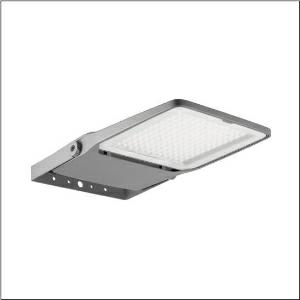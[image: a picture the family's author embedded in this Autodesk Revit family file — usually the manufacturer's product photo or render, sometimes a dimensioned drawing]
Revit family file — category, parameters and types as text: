
# Revit family: floodlight_fl_20_midi___pl52_5xa7682e2d2ac_72a0
name_source: partatom
category: Lighting Fixtures
units: mm (PartAtom-declared; Revit-internal decimal feet)

## family parameters
Cut with Voids When Loaded = No
Host = Face
Light Source = No
Part Type = Normal
Room Calculation Point = No
Round Connector Dimension = Use Diameter
Shared = No

## types (1)
- --- (1 x LED 4000K / CRI = 70 (unbekannt), 26840 lm, 4000K)
    Apparent Load = 208 VA
    CIE Flux Codes = 27 59 98 100 100
    Color Rendering = 70
    Color Temperature = 4000K
    Default Elevation = 1800 mm
    Description = Floodlight FL 20 midi, floodlight, primary light control with lens, of plastic, primary optical cover: protective disc, of toughened safety glass, transparent, light distribution: PL52, light emission: direct distribution, primary light characteristic: asymmetric, installation type: surface-mounted, LED High Power LED, rated luminous flux: 26.840 lm, light colour: 740, colour temperature: 4000K, control gear: ECG Plus, control: flexible luminous flux parameterisation, time-dependent luminous flux control, digital communication interface, power reduction, overheat protection, electronic power reduction, with terminal, 5-pole, max. 2.5mm², mains connection: 220..240V, AC, 50/60Hz, rated input power: 208W, LED unit, of diecast aluminium, powder-coated, Siteco® metallic grey (DB 702S), length: 731 mm, width: 450 mm, height: 76mm, housing frame, of diecast aluminium, powder-coated, Siteco® metallic grey (DB 702S), wall fastening, of steel, powder-coated, Siteco® metallic grey (DB 702S), DALIprotection rating (complete): IP66, insulation class (complete): insulation class II (safety insulation), certification: CE, ENEC, VDE, protection symbol: D, permissible ambient temperature for indoor applications: -40..+40°C, permissible ambient temperature for outdoor applications: -40..+50°C, standard: DIN EN 12944, packaging unit: 1 piece

Light Distribution: PL52
    Height = 76 mm
    Lamp = 1 x LED 4000K / CRI >= 70 (unbekannt)
    Lamp Light Flux = 26840 lm
    Lamp count = 1
    Length = 731 mm
    Luminous efficacy = 129 lm/W
    Manufacturer = Siteco
    ModVariant = No
    Model = 5XA7682E2D2AC
    Number of Poles = 1
    OnlyDefault = Yes
    Power Factor = 1
    Product Name = Floodlight FL 20 midi | PL52
    Product group = floodlight | pylon top
    ProductGroupID = 6101
    Protection Class = Protection class II
    Protection Degree = IP 66
    RLX_Detail_Level = 1
    RlxData = <blob elided: 92061 chars, md5=d3636075>
    Socket = socket
    Standby Power = 0 W
    System Light Flux = 26840 lm
    System Power = 208 W
    Type Comments = factory setting: luminous flux: 100 % | dim-lin: 254 | 484 mA
    Type Image = l_1005944.jpg
    URL = http://relux.com
    VarID = @adj_142933
    Voltage = 0 V
    Weight = 0.00 kg
    Width = 450 mm

## geometry (parser evidence)
native form markers: Blend x4, Sweep x12
no freeform markers — native parametric forms only
